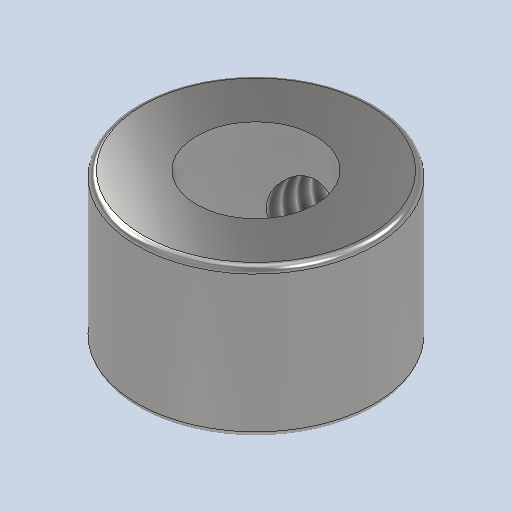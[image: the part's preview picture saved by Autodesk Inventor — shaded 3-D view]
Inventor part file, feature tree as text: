
AUTODESK INVENTOR PART (.ipt)
format: ipt  version: 2022 (Build 260153000, 153)  size: 187,392 bytes
history: native  units: mm
features: sketch x3, extrude x2, fillet x2, other x1, hole x1
ambient origin geometry x8: Origin, YZ Plane, XZ Plane, XY Plane, X Axis, Y Axis, Z Axis, Center Point
bodies: Body1 (feature_tree)
feature tree (9):
  other  "ソリッド1"
  extrude  "押し出し1"  Depth=8.0mm
  fillet  "フィレット1"  Radius=5.0mm
  fillet  "フィレット2"  Radius=0.2mm
  extrude  "押し出し2"  Depth=0.2mm
  hole  "穴1"  [1 undecoded]
  sketch  "スケッチ1"
  sketch  "スケッチ2"
  sketch  "スケッチ3"
note: 1 required parameter value undecoded (feature->parameter linkage not recoverable at this tier; creation-order binding heuristic only, values carry confidence <= 0.55)
